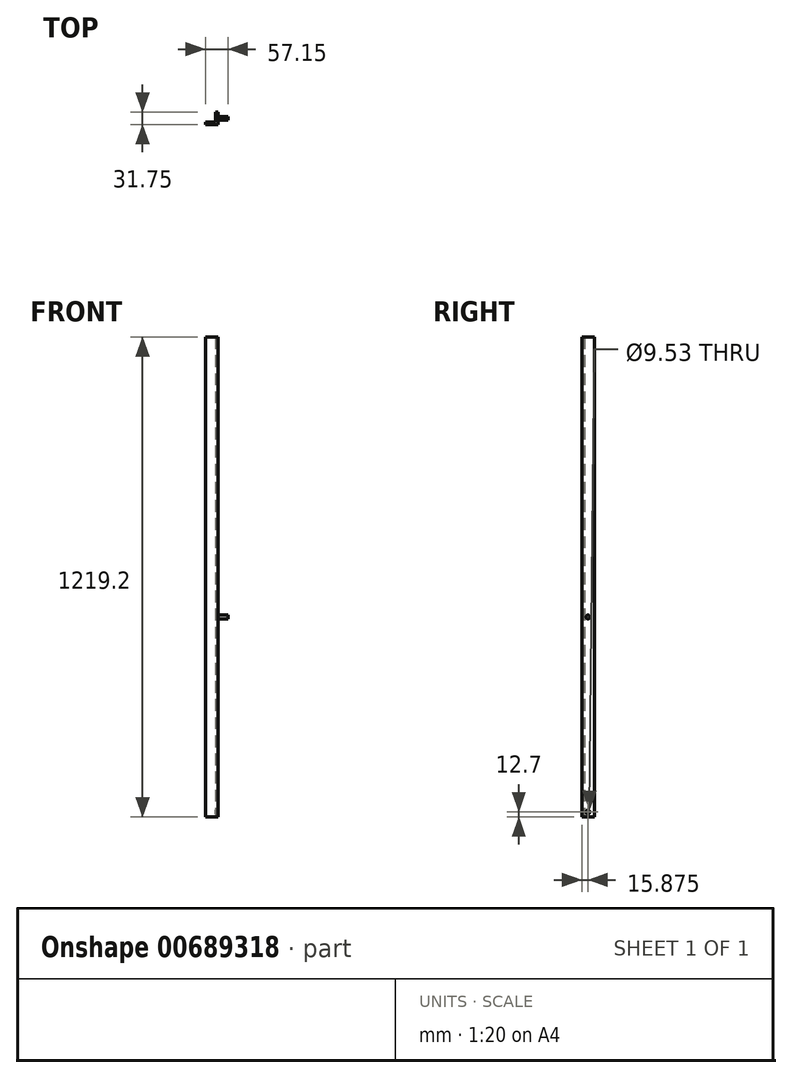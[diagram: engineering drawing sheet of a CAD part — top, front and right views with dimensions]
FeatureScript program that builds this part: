
annotation { "Feature Type Name" : "Feature", "Feature Type Description" : "" }
export const myFeature = defineFeature(function(context is Context, id is Id, definition is map)
    precondition{}
    {
        {
            var Q0;
            Q0=qCreatedBy(makeId("Top.planeOp"),FACE);
            var sketch = newSketch(context, id + "F0", { "sketchPlane" : qUnion([Q0])});
            skLineSegment(sketch, "E0", {"start": v(0, 0) * mm, "end": v(31.75, 0) * mm});
            skLineSegment(sketch, "E1", {"start": v(31.75, 0) * mm, "end": v(31.75, 31.75) * mm});
            skLineSegment(sketch, "E2", {"start": v(31.75, 31.75) * mm, "end": v(25.4, 31.75) * mm});
            skLineSegment(sketch, "E3", {"start": v(25.4, 31.75) * mm, "end": v(25.4, 6.35) * mm});
            skLineSegment(sketch, "E4", {"start": v(25.4, 6.35) * mm, "end": v(0, 6.35) * mm});
            skLineSegment(sketch, "E5", {"start": v(0, 6.35) * mm, "end": v(0, 0) * mm});
            skSolve(sketch);
        }
        {
            var Q0;
            Q0=makeQuery(id+"F0.imprint","IMPRINT",FACE,{"disambiguationData":[TD([[makeQuery(id+"F0.imprint","IMPRINT",EDGE,{"derivedFrom":sQuery(id+"F0.wireOp",EDGE,"E0")}),1.0]])]});
            extrude(context, id + "F1", {"entities" : qUnion([Q0]), "depth" : 1219.2 * mm, "offsetDistance" : 25.4 * mm});
        }
        {
            var Q0;
            Q0=makeQuery(id+"F1.opExtrude","SWEPT_FACE",FACE,{"disambiguationData":[OSD([sQuery(id+"F0.wireOp",EDGE,"E1")])]});
            var sketch = newSketch(context, id + "F2", { "sketchPlane" : qUnion([Q0])});
            skCircle(sketch, "E6", {"center": v(15.88, 12.7) * mm, "radius": 4.76 * mm});
            skSolve(sketch);
        }
        {
            var Q0;
            Q0=makeQuery(id+"F2.imprint","IMPRINT",FACE,{"disambiguationData":[TD([[makeQuery(id+"F2.imprint","IMPRINT",EDGE,{"derivedFrom":sQuery(id+"F2.wireOp",EDGE,"E6")}),1.0]])]});
            extrude(context, id + "F3", {"entities" : qUnion([Q0]), "operationType" : NewBodyOperationType.REMOVE, "endBound" : BoundingType.THROUGH_ALL, "oppositeDirection" : true, "depth" : 25.4 * mm, "offsetDistance" : 25.4 * mm});
        }
        {
            var Q0;
            Q0=makeQuery(id+"F1.opExtrude","SWEPT_FACE",FACE,{"disambiguationData":[OSD([sQuery(id+"F0.wireOp",EDGE,"E1")])]});
            var sketch = newSketch(context, id + "F4", { "sketchPlane" : qUnion([Q0])});
            skCircle(sketch, "E7", {"center": v(15.88, 508) * mm, "radius": 4.76 * mm});
            skSolve(sketch);
        }
        {
            var Q0;
            Q0=makeQuery(id+"F4.imprint","IMPRINT",FACE,{"disambiguationData":[TD([[makeQuery(id+"F4.imprint","IMPRINT",EDGE,{"derivedFrom":sQuery(id+"F4.wireOp",EDGE,"E7")}),1.0]])]});
            extrude(context, id + "F5", {"entities" : qUnion([Q0]), "operationType" : NewBodyOperationType.ADD, "depth" : 25.4 * mm, "offsetDistance" : 25.4 * mm});
        }
    });
